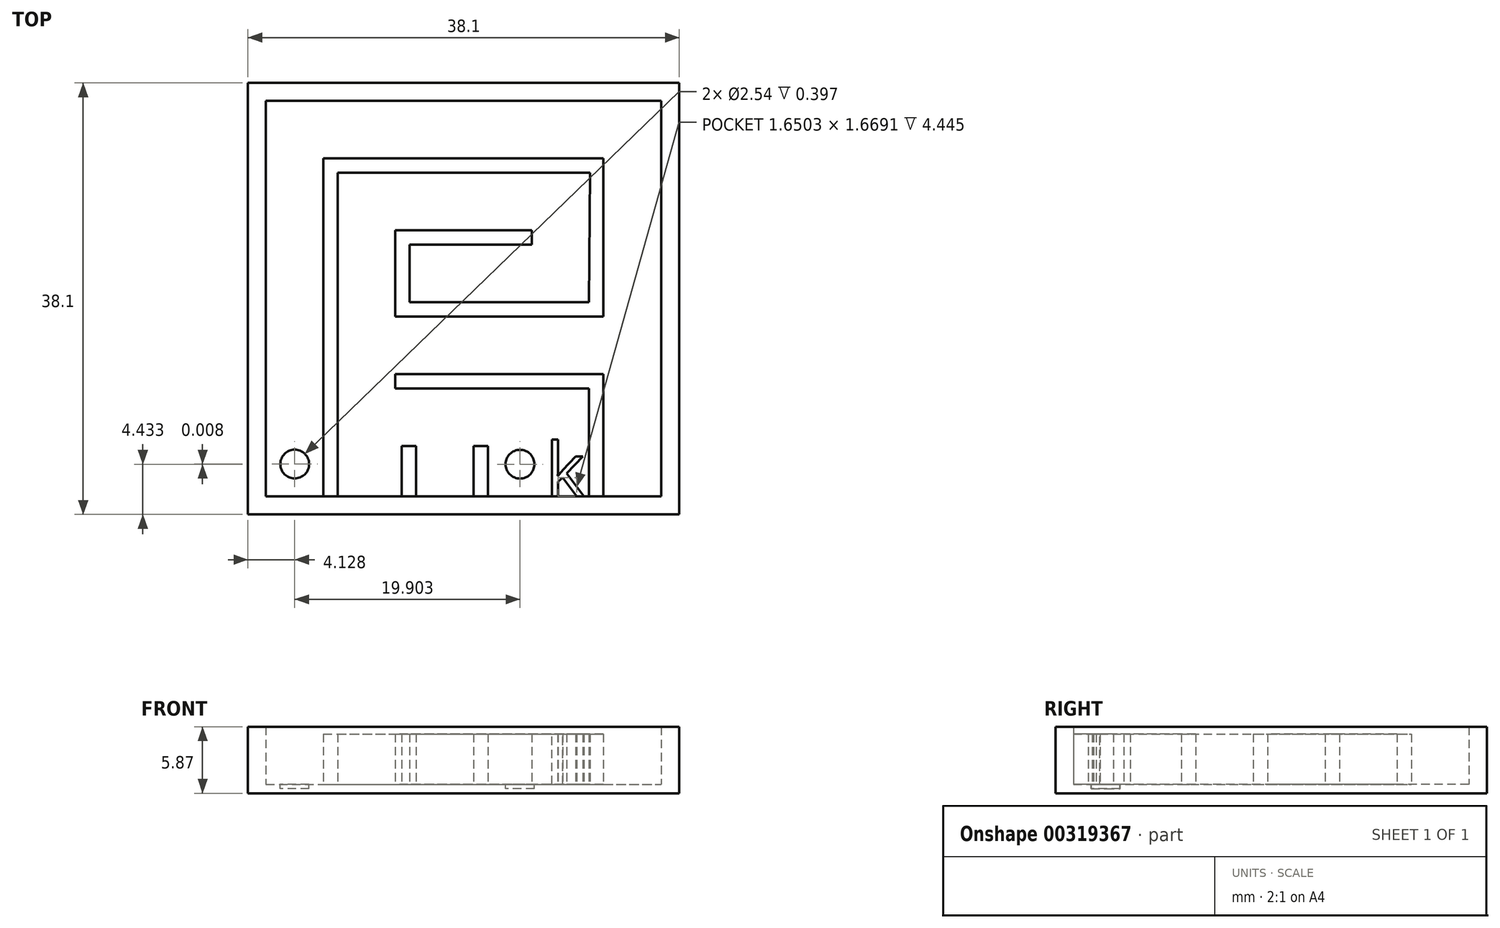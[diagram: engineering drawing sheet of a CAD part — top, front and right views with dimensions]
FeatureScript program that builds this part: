
annotation { "Feature Type Name" : "Feature", "Feature Type Description" : "" }
export const myFeature = defineFeature(function(context is Context, id is Id, definition is map)
    precondition{}
    {
        {
            var Q0;
            Q0=qCreatedBy(makeId("Top.planeOp"),FACE);
            var sketch = newSketch(context, id + "F0", { "sketchPlane" : qUnion([Q0])});
            skLineSegment(sketch, "E0.bottom", {"start": v(-19.29, 22.29) * mm, "end": v(18.81, 22.29) * mm});
            skLineSegment(sketch, "E0.top", {"start": v(-19.29, -15.81) * mm, "end": v(18.81, -15.81) * mm});
            skLineSegment(sketch, "E0.left", {"start": v(-19.29, 22.29) * mm, "end": v(-19.29, -15.81) * mm});
            skLineSegment(sketch, "E0.right", {"start": v(18.81, 22.29) * mm, "end": v(18.81, -15.81) * mm});
            skSolve(sketch);
        }
        {
            var Q0;
            Q0=makeQuery(id+"F0.imprint","IMPRINT",FACE,{"disambiguationData":[TD([[makeQuery(id+"F0.imprint","IMPRINT",EDGE,{"derivedFrom":sQuery(id+"F0.wireOp",EDGE,"E0.bottom")}),-1.0]])]});
            extrude(context, id + "F1", {"entities" : qUnion([Q0]), "depth" : 0.8 * mm});
        }
        {
            var Q0;
            Q0=makeQuery(id+"F1.opExtrude","CAP_FACE",FACE,{"disambiguationData":[OSD([sQuery(id+"F0.wireOp",EDGE,"E0.bottom"),sQuery(id+"F0.wireOp",EDGE,"E0.top"),sQuery(id+"F0.wireOp",EDGE,"E0.left"),sQuery(id+"F0.wireOp",EDGE,"E0.right")])],"isStart":false});
            var sketch = newSketch(context, id + "F2", { "sketchPlane" : qUnion([Q0])});
            skLineSegment(sketch, "E1.0", {"start": v(-17.7, 20.7) * mm, "end": v(17.22, 20.7) * mm});
            skLineSegment(sketch, "E1.1", {"start": v(-17.7, 20.7) * mm, "end": v(-17.7, -14.23) * mm});
            skLineSegment(sketch, "E1.2", {"start": v(-17.7, -14.23) * mm, "end": v(17.22, -14.23) * mm});
            skLineSegment(sketch, "E1.3", {"start": v(17.22, 20.7) * mm, "end": v(17.22, -14.23) * mm});
            skSolve(sketch);
        }
        {
            var Q0;
            Q0=makeQuery(id+"F2.imprint","IMPRINT",FACE,{"disambiguationData":[TD([[makeQuery(id+"F2.imprint","IMPRINT",EDGE,{"derivedFrom":sQuery(id+"F2.wireOp",EDGE,"E1.0")}),1.0]])]});
            extrude(context, id + "F3", {"entities" : qUnion([Q0]), "operationType" : NewBodyOperationType.ADD, "depth" : 5.08 * mm});
        }
        {
            var Q0;
            Q0=makeQuery(id+"F1.opExtrude","CAP_FACE",FACE,{"disambiguationData":[OSD([sQuery(id+"F0.wireOp",EDGE,"E0.bottom"),sQuery(id+"F0.wireOp",EDGE,"E0.top"),sQuery(id+"F0.wireOp",EDGE,"E0.left"),sQuery(id+"F0.wireOp",EDGE,"E0.right")])],"isStart":false});
            var sketch = newSketch(context, id + "F4", { "sketchPlane" : qUnion([Q0])});
            skLineSegment(sketch, "E2.bottom", {"start": v(-12.62, -14.23) * mm, "end": v(-11.35, -14.23) * mm});
            skLineSegment(sketch, "E2.top", {"start": v(-12.62, 15.62) * mm, "end": v(-11.35, 15.62) * mm});
            skLineSegment(sketch, "E2.left", {"start": v(-12.62, -14.23) * mm, "end": v(-12.62, 15.62) * mm});
            skLineSegment(sketch, "E2.right", {"start": v(-11.35, -14.23) * mm, "end": v(-11.35, 15.62) * mm});
            skLineSegment(sketch, "E3.top", {"start": v(-11.35, 14.35) * mm, "end": v(10.93, 14.35) * mm});
            skLineSegment(sketch, "E4.top", {"start": v(12.09, 1.65) * mm, "end": v(10.82, 1.65) * mm});
            skLineSegment(sketch, "E4.right", {"start": v(10.93, 14.35) * mm, "end": v(10.83, 2.92) * mm});
            skLineSegment(sketch, "E5.bottom", {"start": v(10.82, 1.65) * mm, "end": v(-6.27, 1.65) * mm});
            skLineSegment(sketch, "E5.top", {"start": v(10.83, 2.92) * mm, "end": v(-5, 2.92) * mm});
            skLineSegment(sketch, "E5.right", {"start": v(-6.27, 1.65) * mm, "end": v(-6.27, 2.92) * mm});
            skLineSegment(sketch, "E6.top", {"start": v(-6.27, 9.27) * mm, "end": v(-5, 9.27) * mm});
            skLineSegment(sketch, "E6.left", {"start": v(-6.27, 2.92) * mm, "end": v(-6.27, 9.27) * mm});
            skLineSegment(sketch, "E6.right", {"start": v(-5, 2.92) * mm, "end": v(-5, 8) * mm});
            skLineSegment(sketch, "E7.bottom", {"start": v(-5, 9.27) * mm, "end": v(5.8, 9.27) * mm});
            skLineSegment(sketch, "E7.right", {"start": v(5.8, 9.27) * mm, "end": v(5.8, 8) * mm});
            skLineSegment(sketch, "E8", {"start": v(-5, 8) * mm, "end": v(5.8, 8) * mm});
            skLineSegment(sketch, "E9.bottom", {"start": v(12.09, -3.43) * mm, "end": v(10.83, -3.43) * mm});
            skLineSegment(sketch, "E9.top", {"start": v(12.09, -14.23) * mm, "end": v(10.83, -14.23) * mm});
            skLineSegment(sketch, "E9.left", {"start": v(12.09, -3.43) * mm, "end": v(12.09, -14.23) * mm});
            skLineSegment(sketch, "E9.right", {"start": v(10.83, -4.7) * mm, "end": v(10.83, -14.23) * mm});
            skLineSegment(sketch, "E10.bottom", {"start": v(1.92, -14.23) * mm, "end": v(0.65, -14.23) * mm});
            skLineSegment(sketch, "E11.bottom", {"start": v(-4.43, -14.23) * mm, "end": v(-5.7, -14.23) * mm});
            skLineSegment(sketch, "E12", {"start": v(-11.35, 15.62) * mm, "end": v(12.09, 15.62) * mm});
            skPoint(sketch, "E13.end.orphan", {"position": v(12.09, 14.35) * mm});
            skLineSegment(sketch, "E14", {"start": v(12.09, 1.65) * mm, "end": v(12.09, 15.62) * mm});
            skPoint(sketch, "E15.right.start.orphan", {"position": v(-7.37, -3.43) * mm});
            skPoint(sketch, "E15.top.end.orphan", {"position": v(-6.27, -4.7) * mm});
            skLineSegment(sketch, "E16", {"start": v(-6.27, -4.7) * mm, "end": v(10.83, -4.7) * mm});
            skLineSegment(sketch, "E17", {"start": v(10.83, -3.43) * mm, "end": v(-6.27, -3.43) * mm});
            skPoint(sketch, "E10.right.end.orphan", {"position": v(0.65, -9.78) * mm});
            skPoint(sketch, "E11.top.end.orphan", {"position": v(-6.62, -9.78) * mm});
            skLineSegment(sketch, "E18", {"start": v(-6.27, -4.7) * mm, "end": v(-6.27, -3.43) * mm});
            skLineSegment(sketch, "E19.bottom", {"start": v(0.65, -14.23) * mm, "end": v(1.92, -14.23) * mm});
            skLineSegment(sketch, "E19.top", {"start": v(0.65, -9.78) * mm, "end": v(1.92, -9.78) * mm});
            skLineSegment(sketch, "E19.left", {"start": v(0.65, -14.23) * mm, "end": v(0.65, -9.78) * mm});
            skLineSegment(sketch, "E19.right", {"start": v(1.92, -14.23) * mm, "end": v(1.92, -9.78) * mm});
            skLineSegment(sketch, "E20.bottom", {"start": v(-5.7, -14.23) * mm, "end": v(-4.43, -14.23) * mm});
            skLineSegment(sketch, "E20.top", {"start": v(-5.7, -9.78) * mm, "end": v(-4.43, -9.78) * mm});
            skLineSegment(sketch, "E20.left", {"start": v(-5.7, -14.23) * mm, "end": v(-5.7, -9.78) * mm});
            skLineSegment(sketch, "E20.right", {"start": v(-4.43, -14.23) * mm, "end": v(-4.43, -9.78) * mm});
            skText(sketch, "E21", { "text": "k\n", "fontName": "OpenSans-Regular.ttf"});
            const initialGuessF4  = {"E21": [0.007, -0.01423, 1, 0, 0.00476]};
            skSetInitialGuess(sketch, initialGuessF4);
            skSolve(sketch);
        }
        {
            var Q0;
            Q0 = qSketchRegion(id + "F4", true);
            extrude(context, id + "F5", {"entities" : qUnion([Q0]), "operationType" : NewBodyOperationType.ADD, "depth" : 4.44 * mm});
        }
        {
            var Q0;
            Q0=makeQuery(id+"F5.boolean.opBoolean","SPLIT",FACE,{"disambiguationData":[TD([makeQuery(id+"F3.opExtrude","SWEPT_FACE",FACE,{"disambiguationData":[OSD([sQuery(id+"F2.wireOp",EDGE,"E1.0")])]})])],"derivedFrom":makeQuery(id+"F1.opExtrude","CAP_FACE",FACE,{"disambiguationData":[OSD([sQuery(id+"F0.wireOp",EDGE,"E0.bottom"),sQuery(id+"F0.wireOp",EDGE,"E0.top"),sQuery(id+"F0.wireOp",EDGE,"E0.left"),sQuery(id+"F0.wireOp",EDGE,"E0.right")])],"isStart":false})});
            var sketch = newSketch(context, id + "F6", { "sketchPlane" : qUnion([Q0])});
            skLineSegment(sketch, "E22", {"start": v(-17.7, -14.23) * mm, "end": v(-12.62, -14.23) * mm});
            skCircle(sketch, "E23", {"center": v(-15.16, -11.37) * mm, "radius": 1.27 * mm});
            skPoint(sketch, "E23.centerSnap0", {"position": v(-15.16, -14.23) * mm});
            skCircle(sketch, "E24", {"center": v(4.74, -11.38) * mm, "radius": 1.27 * mm});
            skPoint(sketch, "E24.centerSnap0", {"position": v(4.74, -14.23) * mm});
            skSolve(sketch);
        }
        {
            var Q0;
            Q0=makeQuery(id+"F6.imprint","IMPRINT",FACE,{"disambiguationData":[TD([[makeQuery(id+"F6.imprint","IMPRINT",EDGE,{"derivedFrom":sQuery(id+"F6.wireOp",EDGE,"E23")}),1.0]])]});
            var Q1;
            Q1=makeQuery(id+"F6.imprint","IMPRINT",FACE,{"disambiguationData":[TD([[makeQuery(id+"F6.imprint","IMPRINT",EDGE,{"derivedFrom":sQuery(id+"F6.wireOp",EDGE,"E24")}),1.0]])]});
            extrude(context, id + "F7", {"entities" : qUnion([Q0, Q1]), "operationType" : NewBodyOperationType.REMOVE, "oppositeDirection" : true, "depth" : 0.4 * mm});
        }
    });
